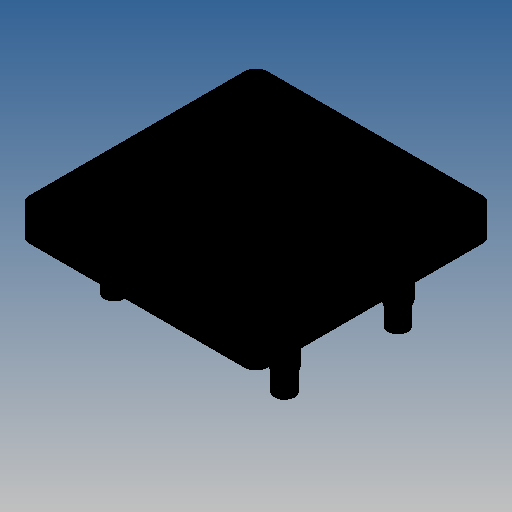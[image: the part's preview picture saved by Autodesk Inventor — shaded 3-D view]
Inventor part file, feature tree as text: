
AUTODESK INVENTOR PART (.ipt)
format: ipt  version: 2020 (Build 240168000, 168)  size: 135,168 bytes
history: native  units: mm (DEFAULTED — no unit token found)
features: other x7, sketch x3, extrude x2, revolve x1, pattern_linear x1
ambient origin geometry x8: Origin, YZ Plane, XZ Plane, XY Plane, X Axis, Y Axis, Z Axis, Center Point
bodies: Solid1 (feature_tree)
feature tree (14):
  extrude  "Extrusion1"  Depth=1.0mm TaperAngle=0.0deg
  extrude  "Extrusion2"  Depth=20.0mm
  revolve  "Revolution1"  [1 undecoded]
  pattern_linear  "Rectangular Pattern1"  [2 undecoded]
  other  "Cap_to_Frame_XY"
  other  "Cap_to_Frame_YZ"
  other  "Cap_to_Frame_ZX"
  other  "Cap_to_Frame_X"
  other  "Cap_to_Frame_Y"
  other  "Cap_to_Frame_Z"
  other  "Cap_to_Frame_Center"
  sketch  "Sketch_1"  dims[d0=2.5mm d1=0.0mm d2=1.0mm d3=0.0mm]
  sketch  "Sketch_2"  dims[d4=360.0deg d5=20.0mm d7=14.3mm d8=20.0mm d10=9.5mm]
  sketch  "Sketch_3"  dims[d11=0.0mm]
note: 3 required parameter values undecoded (feature->parameter linkage not recoverable at this tier; creation-order binding heuristic only, values carry confidence <= 0.55)
